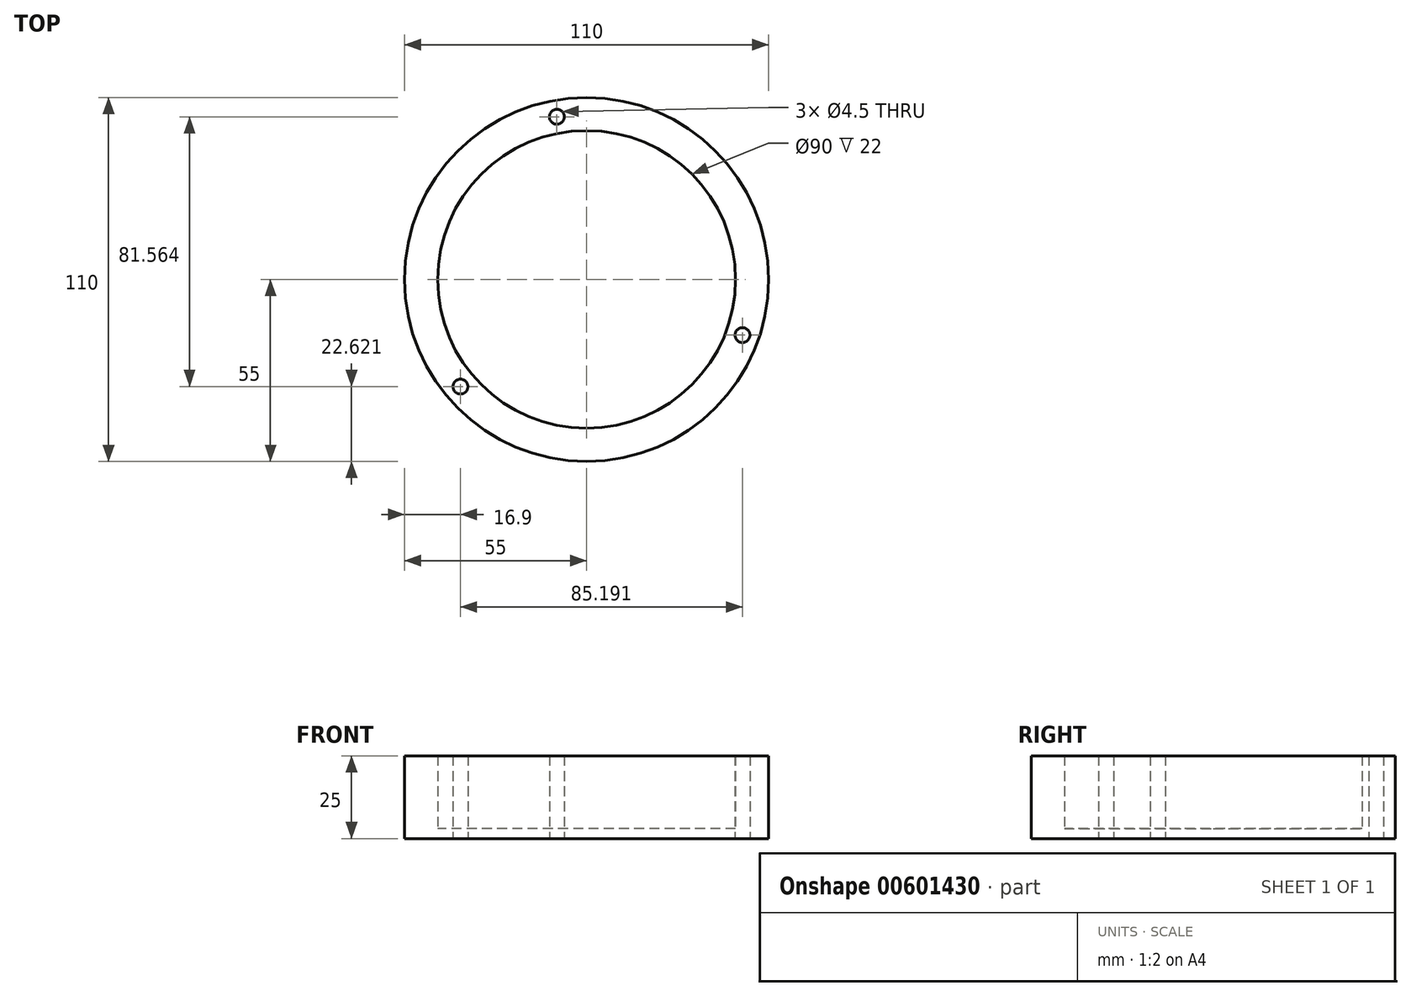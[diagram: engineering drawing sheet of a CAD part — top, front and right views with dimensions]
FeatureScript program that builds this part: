
annotation { "Feature Type Name" : "Feature", "Feature Type Description" : "" }
export const myFeature = defineFeature(function(context is Context, id is Id, definition is map)
    precondition{}
    {
        {
            var Q0;
            Q0=qCreatedBy(makeId("Top.planeOp"),FACE);
            var sketch = newSketch(context, id + "F0", { "sketchPlane" : qUnion([Q0]), "disableImprinting" : false});
            skCircle(sketch, "E0", {"center": v(0, 0) * mm, "radius": 50 * mm});
            skCircle(sketch, "E1", {"center": v(0, 0) * mm, "radius": 55 * mm});
            skCircle(sketch, "E2.cCircle", {"center": v(0, 0) * mm, "radius": 50 * mm, "construction": true});
            skCircle(sketch, "E3", {"center": v(-9, 49.19) * mm, "radius": 2.25 * mm});
            skCircle(sketch, "E4", {"center": v(47.1, -16.8) * mm, "radius": 2.25 * mm});
            skCircle(sketch, "E5", {"center": v(-38.1, -32.38) * mm, "radius": 2.25 * mm});
            skCircle(sketch, "E6", {"center": v(0, 0) * mm, "radius": 45 * mm});
            skSolve(sketch);
        }
        {
            var Q0;
            Q0=makeQuery(id+"F0.imprint","IMPRINT",FACE,{"disambiguationData":[TD([[makeQuery(id+"F0.imprint","IMPRINT",EDGE,{"derivedFrom":sQuery(id+"F0.wireOp",EDGE,"E6")}),-1.0]])]});
            var Q1;
            Q1=makeQuery(id+"F0.imprint","IMPRINT",FACE,{"disambiguationData":[TD([[makeQuery(id+"F0.imprint","IMPRINT",EDGE,{"derivedFrom":sQuery(id+"F0.wireOp",EDGE,"E1")}),1.0]])]});
            extrude(context, id + "F1", {"entities" : qUnion([Q0, Q1]), "flatOperationType" : FlatOperationType.REMOVE, "depth" : 22 * mm, "offsetDistance" : 25 * mm, "domain" : OperationDomain.MODEL});
        }
        {
            var Q0;
            Q0=makeQuery(id+"F0.imprint","IMPRINT",FACE,{"disambiguationData":[TD([[makeQuery(id+"F0.imprint","IMPRINT",EDGE,{"derivedFrom":sQuery(id+"F0.wireOp",EDGE,"E6")}),1.0]])]});
            var Q1;
            Q1=makeQuery(id+"F0.imprint","IMPRINT",FACE,{"disambiguationData":[TD([[makeQuery(id+"F0.imprint","IMPRINT",EDGE,{"derivedFrom":sQuery(id+"F0.wireOp",EDGE,"E6")}),-1.0]])]});
            var Q2;
            Q2=makeQuery(id+"F0.imprint","IMPRINT",FACE,{"disambiguationData":[TD([[makeQuery(id+"F0.imprint","IMPRINT",EDGE,{"derivedFrom":sQuery(id+"F0.wireOp",EDGE,"E1")}),1.0]])]});
            extrude(context, id + "F2", {"entities" : qUnion([Q0, Q1, Q2]), "operationType" : NewBodyOperationType.ADD, "flatOperationType" : FlatOperationType.REMOVE, "oppositeDirection" : true, "depth" : 3 * mm, "offsetDistance" : 25 * mm, "domain" : OperationDomain.MODEL});
        }
    });
